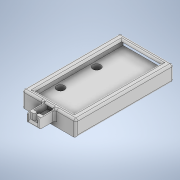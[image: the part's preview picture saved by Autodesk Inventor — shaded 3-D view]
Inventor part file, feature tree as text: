
AUTODESK INVENTOR PART (.ipt)
format: ipt  version: 2020 (Build 240168000, 168)  size: 327,680 bytes
history: native  units: in
note: dims shown in document units (in); Inventor stores cm internally (conversion verified against a paired STEP export)
features: extrude x11, sketch x10, fillet x1
ambient origin geometry x8: Origin, YZ Plane, XZ Plane, XY Plane, X Axis, Y Axis, Z Axis, Center Point
bodies: Solid1 (feature_tree)
feature tree (22):
  sketch  "Sketch1"  dims[d0=5.8in d1=3.0in]
  sketch  "Sketch2"  dims[d2=3.4in d3=6.2in]
  extrude  "Extrusion1"  Depth=3.0in
  extrude  "Extrusion2"  Depth=6.2in
  extrude  "Extrusion3"  Depth=3.4in
  extrude  "Extrusion5"  Depth=0.5in
  extrude  "Extrusion7"  Depth=0.5in TaperAngle=0.0deg
  extrude  "Extrusion8"  Depth=0.5in
  extrude  "Extrusion9"  Depth=0.3in TaperAngle=0.0deg
  extrude  "Extrusion10"  Depth=0.1in
  fillet  "Fillet1"  Radius=0.1in
  extrude  "Extrusion12"  Depth=1.0in TaperAngle=0.0deg
  extrude  "Extrusion13"  Depth=0.1in TaperAngle=0.0deg
  extrude  "Extrusion14"  Depth=0.5in
  sketch  "Sketch3"  dims[d4=3.4in d5=3.4in]
  sketch  "Sketch5"  dims[d6=1.3in d8=0.5in]
  sketch  "Sketch6"  dims[d9=0.5in d10=0.0in d11=6.2in d12=0.0in]
  sketch  "Sketch7"  dims[d13=0.5in d14=0.0in d17=0.6in]
  sketch  "Sketch8"  dims[d18=0.3in d19=0.2in d20=0.0in]
  sketch  "Sketch10"  dims[d23=2.5in d24=5.5in d25=0.1in d26=0.0in]
  sketch  "Sketch12"  dims[d27=0.75in d28=1.0in d29=0.0in]
  sketch  "Sketch13"  dims[d30=0.1in d31=0.0in d32=0.1in d33=0.0in d34=0.125in d37=0.15in d38=0.2in d39=0.15in d40=0.1in d41=0.1in d42=0.4in d43=0.0in d45=0.2in d46=0.2in d47=0.2in d48=0.2in d49=2.29in d50=2.29in d51=2.29in d52=1.0in d53=0.0in d54=0.5in d55=0.5in d56=0.5in d57=0.5in d58=0.3in d59=0.0in d15=0.5in d16=0.0344in d44=0.5in]
